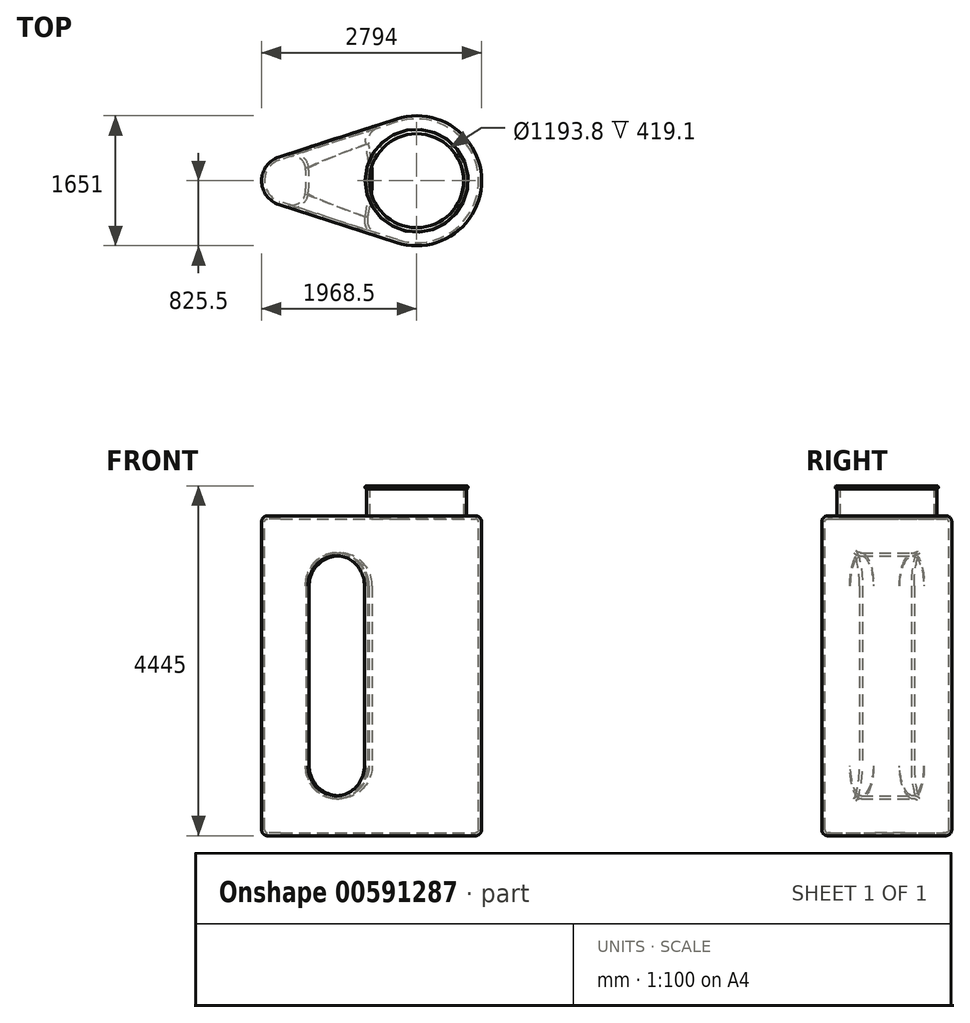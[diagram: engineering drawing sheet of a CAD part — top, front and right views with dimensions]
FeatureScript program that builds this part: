
annotation { "Feature Type Name" : "Feature", "Feature Type Description" : "" }
export const myFeature = defineFeature(function(context is Context, id is Id, definition is map)
    precondition{}
    {
        {
            var Q0;
            Q0=qCreatedBy(makeId("Top.planeOp"),FACE);
            var sketch = newSketch(context, id + "F0", { "sketchPlane" : qUnion([Q0])});
            skArc(sketch, "E0", {"start": v(-254, -785.45) * mm, "mid": v(825.5, 0) * mm, "end": v(-254, 785.45) * mm});
            skArc(sketch, "E1", {"start": v(-1748.7, 302.1) * mm, "mid": v(-1968.5, 0) * mm, "end": v(-1748.7, -302.1) * mm});
            skLineSegment(sketch, "E2", {"start": v(-254, 785.45) * mm, "end": v(-1748.7, 302.1) * mm});
            skLineSegment(sketch, "E3", {"start": v(-254, -785.45) * mm, "end": v(-1748.7, -302.1) * mm});
            skPoint(sketch, "E4.orphan", {"position": v(0, 825.5) * mm});
            skSolve(sketch);
        }
        {
            var Q0;
            Q0=makeQuery(id+"F0.imprint","IMPRINT",FACE,{"disambiguationData":[TD([[makeQuery(id+"F0.imprint","IMPRINT",EDGE,{"derivedFrom":sQuery(id+"F0.wireOp",EDGE,"E0")}),1.0]])]});
            extrude(context, id + "F1", {"entities" : qUnion([Q0]), "oppositeDirection" : true, "depth" : 4064 * mm, "offsetDistance" : 25.4 * mm});
        }
        {
            var Q0;
            Q0=makeQuery(id+"F1.opExtrude","SWEPT_FACE",FACE,{"disambiguationData":[OSD([sQuery(id+"F0.wireOp",EDGE,"E3")])]});
            var sketch = newSketch(context, id + "F2", { "sketchPlane" : qUnion([Q0])});
            skArc(sketch, "E5", {"start": v(-476, -889) * mm, "mid": v(-857, -508) * mm, "end": v(-1238, -889) * mm});
            skArc(sketch, "E6", {"start": v(-1238, -3175) * mm, "mid": v(-857, -3556) * mm, "end": v(-476, -3175) * mm});
            skLineSegment(sketch, "E7", {"start": v(-476, -889) * mm, "end": v(-476, -3175) * mm});
            skLineSegment(sketch, "E8", {"start": v(-1238, -889) * mm, "end": v(-1238, -3175) * mm});
            skLineSegment(sketch, "E9", {"start": v(-2635, 0) * mm, "end": v(-2635, -4064) * mm});
            skSolve(sketch);
        }
        {
            var Q0;
            Q0 = qSketchRegion(id + "F2", true);
            var Q1;
            Q1=sQuery(id+"F2.wireOp",EDGE,"E9");
            revolve(context, id + "F3", {"operationType" : NewBodyOperationType.REMOVE, "entities" : qUnion([Q0]), "axis" : qUnion([Q1]), "revolveType" : RevolveType.FULL, "oppositeDirection" : true});
        }
        {
            var Q0;
            Q0=makeQuery(id+"F1.opExtrude","CAP_FACE",FACE,{"disambiguationData":[OSD([sQuery(id+"F0.wireOp",EDGE,"E0"),sQuery(id+"F0.wireOp",EDGE,"E1"),sQuery(id+"F0.wireOp",EDGE,"E2"),sQuery(id+"F0.wireOp",EDGE,"E3")])],"isStart":true});
            var sketch = newSketch(context, id + "F4", { "sketchPlane" : qUnion([Q0])});
            skCircle(sketch, "E10", {"center": v(0, 0) * mm, "radius": 635 * mm});
            skSolve(sketch);
        }
        {
            var Q0;
            Q0=makeQuery(id+"F4.imprint","IMPRINT",FACE,{"disambiguationData":[TD([[makeQuery(id+"F4.imprint","IMPRINT",EDGE,{"derivedFrom":sQuery(id+"F4.wireOp",EDGE,"E10")}),1.0]])]});
            extrude(context, id + "F5", {"entities" : qUnion([Q0]), "operationType" : NewBodyOperationType.ADD, "depth" : 381 * mm, "offsetDistance" : 25.4 * mm});
        }
        {
            var Q0;
            Q0=makeQuery(id+"F3.boolean.opBoolean","INTERSECT",EDGE,{"derivedFrom":[makeQuery(id+"F1.opExtrude","SWEPT_FACE",FACE,{"disambiguationData":[OSD([sQuery(id+"F0.wireOp",EDGE,"E3")])]}),makeQuery(id+"F3.opRevolve","SWEPT_FACE",FACE,{"disambiguationData":[OSD([sQuery(id+"F2.wireOp",EDGE,"E8")])]})]});
            var Q1;
            Q1=makeQuery(id+"F3.boolean.opBoolean","INTERSECT",EDGE,{"derivedFrom":[makeQuery(id+"F1.opExtrude","SWEPT_FACE",FACE,{"disambiguationData":[OSD([sQuery(id+"F0.wireOp",EDGE,"E2")])]}),makeQuery(id+"F3.opRevolve","SWEPT_FACE",FACE,{"disambiguationData":[OSD([sQuery(id+"F2.wireOp",EDGE,"E7")])]})]});
            fillet(context, id + "F6", {"entities" : qUnion([Q0, Q1]), "radius" : 203.2 * mm, "tangentPropagation" : true, "allowEdgeOverflow" : false});
        }
        {
            var Q0;
            Q0=makeQuery(id+"F1.opExtrude","CAP_EDGE",EDGE,{"disambiguationData":[OSD([sQuery(id+"F0.wireOp",EDGE,"E3")])],"isStart":true});
            var Q1;
            Q1=makeQuery(id+"F1.opExtrude","CAP_EDGE",EDGE,{"disambiguationData":[OSD([sQuery(id+"F0.wireOp",EDGE,"E0")])],"isStart":false});
            fillet(context, id + "F7", {"entities" : qUnion([Q0, Q1]), "radius" : 76.2 * mm, "tangentPropagation" : true, "allowEdgeOverflow" : false});
        }
        {
            var Q0;
            Q0=makeQuery(id+"F5.opExtrude","CAP_FACE",FACE,{"disambiguationData":[OSD([sQuery(id+"F4.wireOp",EDGE,"E10")])],"isStart":false});
            shell(context, id + "F8", {"entities" : qUnion([Q0]), "thickness" : 38.1 * mm});
        }
        {
            var Q0;
            Q0=qCreatedBy(makeId("Front.planeOp"),FACE);
            var sketch = newSketch(context, id + "F9", { "sketchPlane" : qUnion([Q0])});
            skLineSegment(sketch, "E11", {"start": v(0, 162.61) * mm, "end": v(0, 602.53) * mm, "construction": true});
            skLineSegment(sketch, "E12", {"start": v(635, 259.04) * mm, "end": v(635, 453.46) * mm, "construction": true});
            skCircle(sketch, "E13", {"center": v(635, 361.95) * mm, "radius": 19.05 * mm});
            skSolve(sketch);
        }
        {
            var Q0;
            Q0 = qSketchRegion(id + "F9", true);
            var Q1;
            Q1=sQuery(id+"F9.wireOp",EDGE,"E11");
            revolve(context, id + "F10", {"operationType" : NewBodyOperationType.ADD, "entities" : qUnion([Q0]), "axis" : qUnion([Q1]), "revolveType" : RevolveType.FULL});
        }
    });
